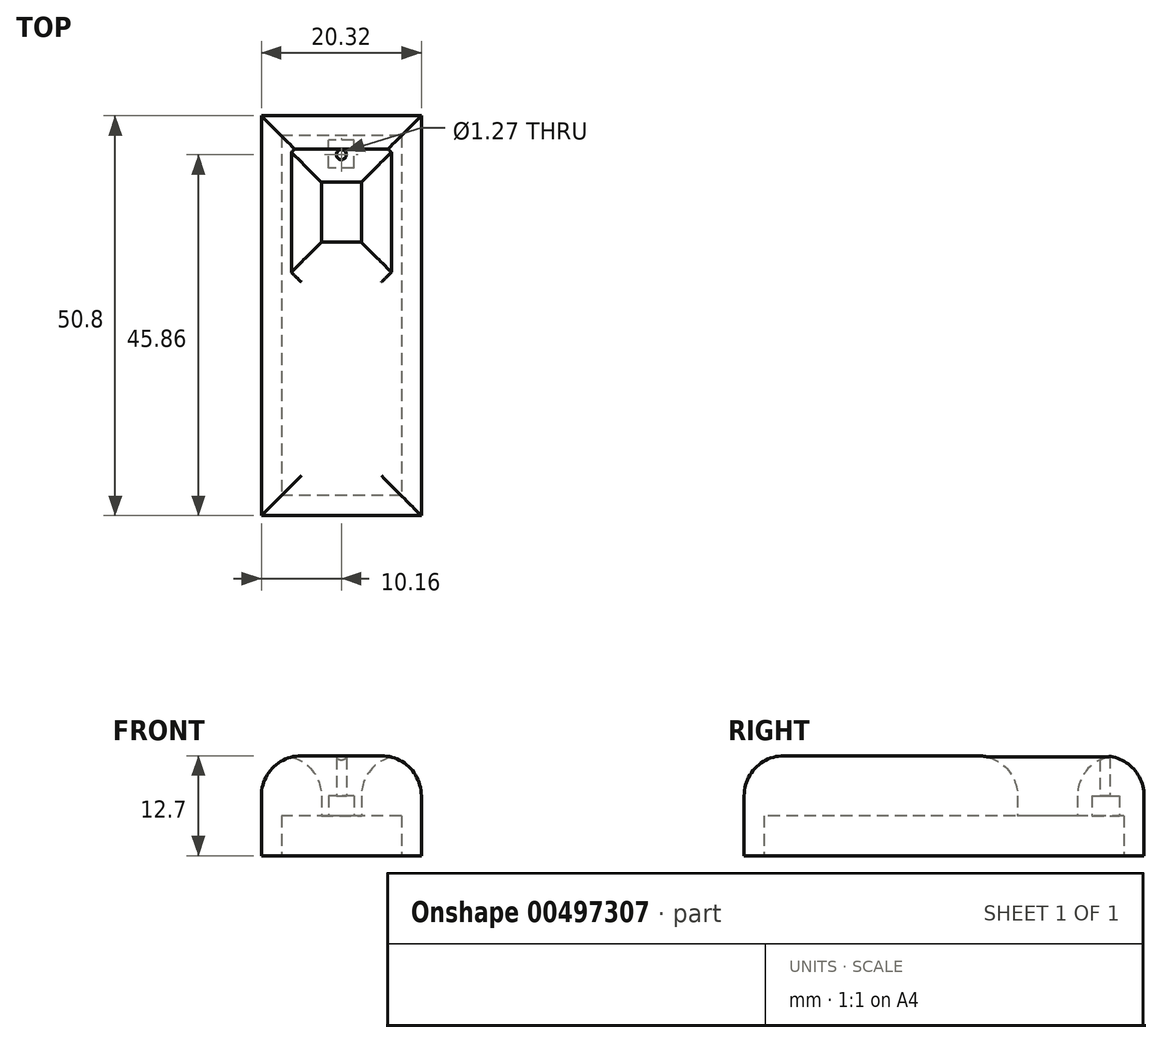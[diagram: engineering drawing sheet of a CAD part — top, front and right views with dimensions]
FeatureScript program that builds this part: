
annotation { "Feature Type Name" : "Feature", "Feature Type Description" : "" }
export const myFeature = defineFeature(function(context is Context, id is Id, definition is map)
    precondition{}
    {
        {
            var Q0;
            Q0=qCreatedBy(makeId("Top.planeOp"),FACE);
            var sketch = newSketch(context, id + "F0", { "sketchPlane" : qUnion([Q0])});
            skLineSegment(sketch, "E0.bottom", {"start": v(10.16, 25.4) * mm, "end": v(-10.16, 25.4) * mm});
            skLineSegment(sketch, "E0.top", {"start": v(10.16, -25.4) * mm, "end": v(-10.16, -25.4) * mm});
            skLineSegment(sketch, "E0.left", {"start": v(10.16, 25.4) * mm, "end": v(10.16, -25.4) * mm});
            skLineSegment(sketch, "E0.right", {"start": v(-10.16, 25.4) * mm, "end": v(-10.16, -25.4) * mm});
            skSolve(sketch);
        }
        {
            var Q0;
            Q0=makeQuery(id+"F0.imprint","IMPRINT",FACE,{"disambiguationData":[TD([[makeQuery(id+"F0.imprint","IMPRINT",EDGE,{"derivedFrom":sQuery(id+"F0.wireOp",EDGE,"E0.bottom")}),1.0]])]});
            extrude(context, id + "F1", {"entities" : qUnion([Q0]), "depth" : 12.7 * mm});
        }
        {
            var Q0;
            Q0=qCreatedBy(makeId("Top.planeOp"),FACE);
            var sketch = newSketch(context, id + "F2", { "sketchPlane" : qUnion([Q0])});
            skLineSegment(sketch, "E1.bottom", {"start": v(7.62, 22.86) * mm, "end": v(-7.62, 22.86) * mm});
            skLineSegment(sketch, "E1.top", {"start": v(7.62, -22.86) * mm, "end": v(-7.62, -22.86) * mm});
            skLineSegment(sketch, "E1.left", {"start": v(7.62, 22.86) * mm, "end": v(7.62, -22.86) * mm});
            skLineSegment(sketch, "E1.right", {"start": v(-7.62, 22.86) * mm, "end": v(-7.62, -22.86) * mm});
            skSolve(sketch);
        }
        {
            var Q0;
            Q0 = qSketchRegion(id + "F2", true);
            extrude(context, id + "F3", {"entities" : qUnion([Q0]), "operationType" : NewBodyOperationType.REMOVE, "depth" : 5.08 * mm});
        }
        {
            var Q0;
            Q0=makeQuery(id+"F3.boolean.opBoolean","COPY",FACE,{"derivedFrom":makeQuery(id+"F3.opExtrude","CAP_FACE",FACE,{"disambiguationData":[OSD([sQuery(id+"F2.wireOp",EDGE,"E1.bottom"),sQuery(id+"F2.wireOp",EDGE,"E1.top"),sQuery(id+"F2.wireOp",EDGE,"E1.left"),sQuery(id+"F2.wireOp",EDGE,"E1.right")])],"isStart":false})});
            var sketch = newSketch(context, id + "F4", { "sketchPlane" : qUnion([Q0])});
            skLineSegment(sketch, "E2.bottom", {"start": v(1.6, -18.78) * mm, "end": v(-1.6, -18.78) * mm});
            skLineSegment(sketch, "E2.top", {"start": v(1.6, -22.29) * mm, "end": v(-1.6, -22.29) * mm});
            skLineSegment(sketch, "E2.left", {"start": v(1.6, -18.78) * mm, "end": v(1.6, -22.29) * mm});
            skLineSegment(sketch, "E2.right", {"start": v(-1.6, -18.78) * mm, "end": v(-1.6, -22.29) * mm});
            skPoint(sketch, "E3", {"position": v(0, -18.78) * mm});
            skSolve(sketch);
        }
        {
            var Q0;
            Q0=makeQuery(id+"F4.imprint","IMPRINT",FACE,{"disambiguationData":[TD([[makeQuery(id+"F4.imprint","IMPRINT",EDGE,{"derivedFrom":sQuery(id+"F4.wireOp",EDGE,"E2.bottom")}),1.0]])]});
            extrude(context, id + "F5", {"entities" : qUnion([Q0]), "operationType" : NewBodyOperationType.REMOVE, "oppositeDirection" : true, "depth" : 2.54 * mm});
        }
        {
            var Q0;
            Q0=qCreatedBy(makeId("Top.planeOp"),FACE);
            var sketch = newSketch(context, id + "F6", { "sketchPlane" : qUnion([Q0])});
            skLineSegment(sketch, "E4.bottom", {"start": v(2.54, 9.33) * mm, "end": v(-2.54, 9.33) * mm});
            skLineSegment(sketch, "E4.top", {"start": v(2.54, 16.95) * mm, "end": v(-2.54, 16.95) * mm});
            skLineSegment(sketch, "E4.left", {"start": v(2.54, 9.33) * mm, "end": v(2.54, 16.95) * mm});
            skLineSegment(sketch, "E4.right", {"start": v(-2.54, 9.33) * mm, "end": v(-2.54, 16.95) * mm});
            skPoint(sketch, "E5", {"position": v(0, 16.95) * mm});
            skSolve(sketch);
        }
        {
            var Q0;
            Q0 = qSketchRegion(id + "F6", true);
            var Q1;
            Q1=makeQuery(id+"F6.imprint","IMPRINT",FACE,{"disambiguationData":[TD([[makeQuery(id+"F6.imprint","IMPRINT",EDGE,{"derivedFrom":sQuery(id+"F6.wireOp",EDGE,"E4.bottom")}),-1.0]])]});
            extrude(context, id + "F7", {"entities" : qUnion([Q0, Q1]), "operationType" : NewBodyOperationType.REMOVE, "depth" : 25.4 * mm});
        }
        {
            var Q0;
            Q0=makeQuery(id+"F1.opExtrude","CAP_FACE",FACE,{"disambiguationData":[OSD([sQuery(id+"F0.wireOp",EDGE,"E0.bottom"),sQuery(id+"F0.wireOp",EDGE,"E0.top"),sQuery(id+"F0.wireOp",EDGE,"E0.left"),sQuery(id+"F0.wireOp",EDGE,"E0.right")])],"isStart":false});
            fillet(context, id + "F8", {"entities" : qUnion([Q0]), "radius" : 5.08 * mm, "tangentPropagation" : true, "allowEdgeOverflow" : false});
        }
        {
            var Q0;
            Q0=makeQuery(id+"F5.boolean.opBoolean","COPY",FACE,{"derivedFrom":makeQuery(id+"F5.opExtrude","CAP_FACE",FACE,{"disambiguationData":[OSD([sQuery(id+"F4.wireOp",EDGE,"E2.bottom"),sQuery(id+"F4.wireOp",EDGE,"E2.top"),sQuery(id+"F4.wireOp",EDGE,"E2.left"),sQuery(id+"F4.wireOp",EDGE,"E2.right")])],"isStart":false})});
            var sketch = newSketch(context, id + "F9", { "sketchPlane" : qUnion([Q0])});
            skCircle(sketch, "E6", {"center": v(0, -20.46) * mm, "radius": 0.64 * mm});
            skSolve(sketch);
        }
        {
            var Q0;
            Q0 = qSketchRegion(id + "F9", true);
            extrude(context, id + "F10", {"entities" : qUnion([Q0]), "operationType" : NewBodyOperationType.REMOVE, "oppositeDirection" : true, "depth" : 25.4 * mm});
        }
    });
